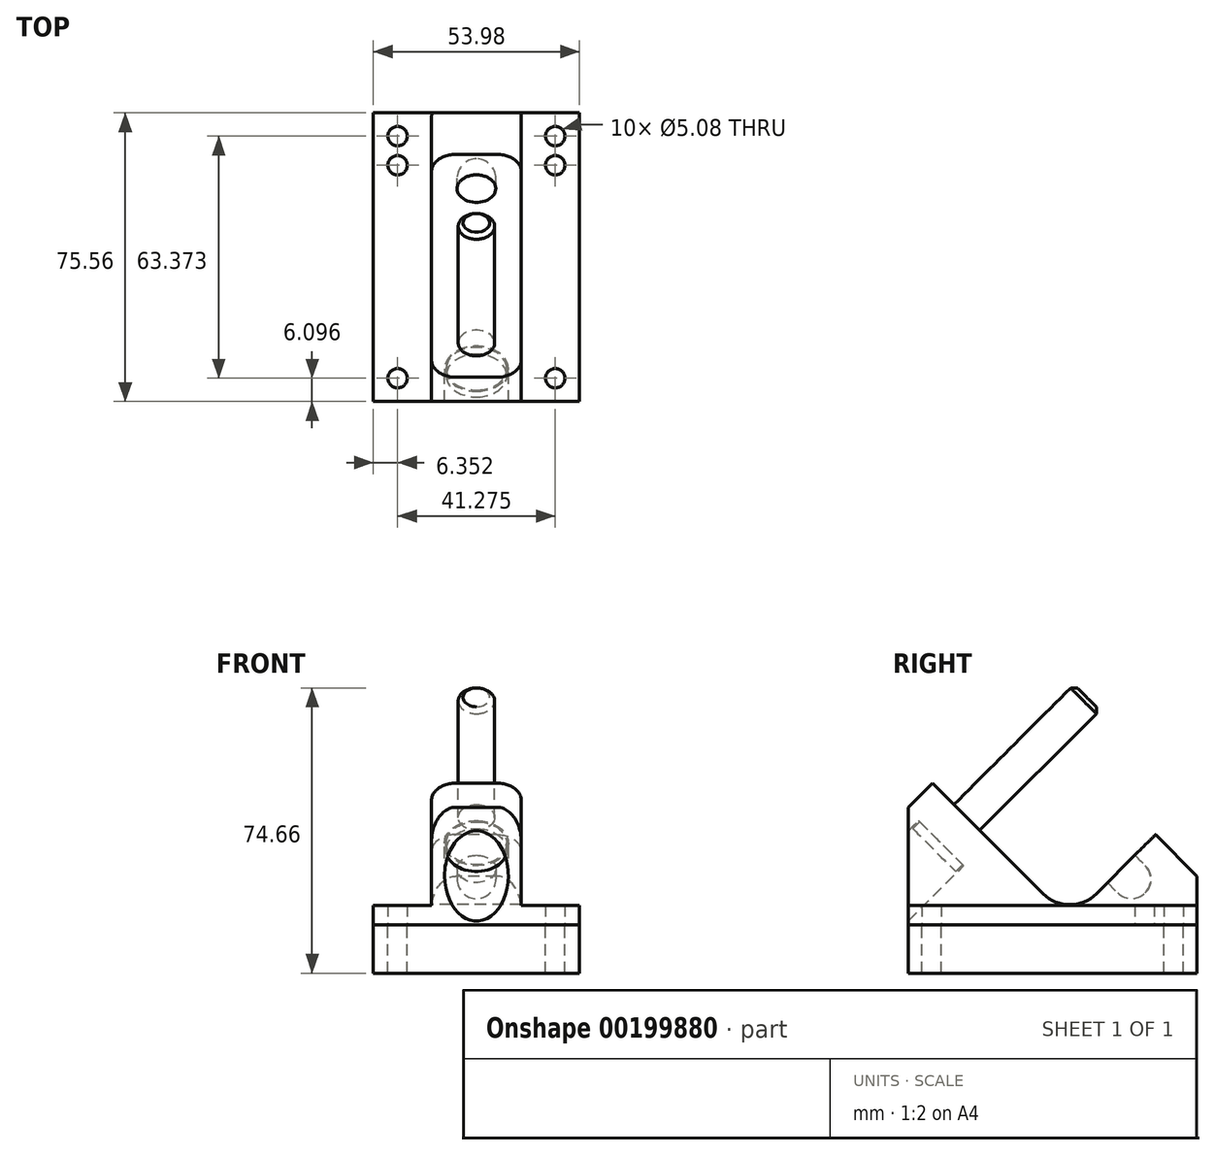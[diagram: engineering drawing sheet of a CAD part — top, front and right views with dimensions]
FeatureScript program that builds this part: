
annotation { "Feature Type Name" : "Feature", "Feature Type Description" : "" }
export const myFeature = defineFeature(function(context is Context, id is Id, definition is map)
    precondition{}
    {
        {
            var Q0;
            Q0=qCreatedBy(makeId("Right.planeOp"),FACE);
            var sketch = newSketch(context, id + "F0", { "sketchPlane" : qUnion([Q0])});
            skLineSegment(sketch, "E0", {"start": v(0, 0) * mm, "end": v(75.57, 0) * mm});
            skLineSegment(sketch, "E1", {"start": v(75.57, 0) * mm, "end": v(75.57, 12.7) * mm});
            skLineSegment(sketch, "E2", {"start": v(75.57, 12.7) * mm, "end": v(64.7, 23.57) * mm});
            skLineSegment(sketch, "E3", {"start": v(64.7, 23.57) * mm, "end": v(42.25, 1.12) * mm});
            skLineSegment(sketch, "E4", {"start": v(0, -14.12) * mm, "end": v(0, 0) * mm, "construction": true});
            skLineSegment(sketch, "E5", {"start": v(0, 0) * mm, "end": v(0, 30.72) * mm});
            skLineSegment(sketch, "E6", {"start": v(0, 30.72) * mm, "end": v(6.32, 37.04) * mm});
            skLineSegment(sketch, "E7", {"start": v(6.32, 37.04) * mm, "end": v(42.25, 1.12) * mm});
            skLineSegment(sketch, "E8", {"start": v(61.1, 19.98) * mm, "end": v(70.08, 11) * mm, "construction": true});
            skLineSegment(sketch, "E9", {"start": v(70.08, 11) * mm, "end": v(59.3, 0.22) * mm, "construction": true});
            skLineSegment(sketch, "E10", {"start": v(59.3, 0.22) * mm, "end": v(50.33, 9.2) * mm, "construction": true});
            skLineSegment(sketch, "E11", {"start": v(64.7, 5.6) * mm, "end": v(15.3, 55) * mm, "construction": true});
            skCircle(sketch, "E12", {"center": v(15.3, 55) * mm, "radius": 4 * mm, "construction": true});
            skLineSegment(sketch, "E13", {"start": v(15.3, 28.06) * mm, "end": v(28.77, 41.53) * mm, "construction": true});
            skCircle(sketch, "E14", {"center": v(58.4, 11.9) * mm, "radius": 5.08 * mm, "construction": true});
            skSolve(sketch);
        }
        {
            var Q0;
            Q0=qSketchRegion(id+"F0",true);
            extrude(context, id + "F1", {"entities" : qUnion([Q0]), "depth" : 26.99 * mm});
        }
        {
            var Q0;
            Q0=makeQuery(id+"F1.opExtrude","SWEPT_EDGE",EDGE,{"disambiguationData":[OSD([sQuery(id+"F0.wireOp",EDGE,"E3"),sQuery(id+"F0.wireOp",EDGE,"E7")])]});
            fillet(context, id + "F2", {"entities" : qUnion([Q0]), "radius" : 9.9 * mm, "tangentPropagation" : true, "allowEdgeOverflow" : false});
        }
        {
            var Q0;
            Q0=makeQuery(id+"F1.opExtrude","CAP_FACE",FACE,{"disambiguationData":[OSD([sQuery(id+"F0.wireOp",EDGE,"E0"),sQuery(id+"F0.wireOp",EDGE,"E1"),sQuery(id+"F0.wireOp",EDGE,"E2"),sQuery(id+"F0.wireOp",EDGE,"E3"),sQuery(id+"F0.wireOp",EDGE,"O8t1L6aE-7V4B-qQYz-aJHa-yxt4Uf4GNHZm"),sQuery(id+"F0.wireOp",EDGE,"dINw5n4X-CGaa-rPGi-QK1T-MrZfrRMsY7ox"),sQuery(id+"F0.wireOp",EDGE,"k2Hi1M4v-dZXO-cidX-ee3S-7WINr6mVTnzP")])],"isStart":false});
            var sketch = newSketch(context, id + "F3", { "sketchPlane" : qUnion([Q0])});
            skLineSegment(sketch, "E15.bottom", {"start": v(75.57, 5.08) * mm, "end": v(0, 5.08) * mm});
            skLineSegment(sketch, "E15.top", {"start": v(75.57, 37.04) * mm, "end": v(0, 37.04) * mm});
            skLineSegment(sketch, "E15.left", {"start": v(75.57, 5.08) * mm, "end": v(75.57, 37.04) * mm});
            skLineSegment(sketch, "E15.right", {"start": v(0, 5.08) * mm, "end": v(0, 37.04) * mm});
            skSolve(sketch);
        }
        {
            var Q0;
            Q0=qSketchRegion(id+"F3",true);
            extrude(context, id + "F4", {"entities" : qUnion([Q0]), "operationType" : NewBodyOperationType.REMOVE, "oppositeDirection" : true, "depth" : 15.24 * mm});
        }
        {
            var Q0;
            Q0=makeQuery(id+"F1.opExtrude","SWEPT_FACE",FACE,{"disambiguationData":[OSD([sQuery(id+"F0.wireOp",EDGE,"E0")])]});
            var sketch = newSketch(context, id + "F5", { "sketchPlane" : qUnion([Q0])});
            skLineSegment(sketch, "E16", {"start": v(20.64, -6.1) * mm, "end": v(20.64, -61.85) * mm, "construction": true});
            skLineSegment(sketch, "E17", {"start": v(20.64, -61.85) * mm, "end": v(20.64, -69.47) * mm, "construction": true});
            skCircle(sketch, "E18", {"center": v(20.64, -6.1) * mm, "radius": 2.54 * mm});
            skCircle(sketch, "E19", {"center": v(20.64, -61.85) * mm, "radius": 2.54 * mm});
            skCircle(sketch, "E20", {"center": v(20.64, -69.47) * mm, "radius": 2.54 * mm});
            skSolve(sketch);
        }
        {
            var Q0;
            Q0=qSketchRegion(id+"F5",true);
            extrude(context, id + "F6", {"entities" : qUnion([Q0]), "operationType" : NewBodyOperationType.REMOVE, "endBound" : BoundingType.UP_TO_NEXT, "oppositeDirection" : true, "depth" : 25.4 * mm});
        }
        {
            var Q0;
            Q0=makeQuery(id+"F1.opExtrude","CAP_FACE",FACE,{"disambiguationData":[OSD([sQuery(id+"F0.wireOp",EDGE,"E0"),sQuery(id+"F0.wireOp",EDGE,"E1"),sQuery(id+"F0.wireOp",EDGE,"E2"),sQuery(id+"F0.wireOp",EDGE,"E3"),sQuery(id+"F0.wireOp",EDGE,"O8t1L6aE-7V4B-qQYz-aJHa-yxt4Uf4GNHZm"),sQuery(id+"F0.wireOp",EDGE,"dINw5n4X-CGaa-rPGi-QK1T-MrZfrRMsY7ox"),sQuery(id+"F0.wireOp",EDGE,"k2Hi1M4v-dZXO-cidX-ee3S-7WINr6mVTnzP")])],"isStart":true});
            var sketch = newSketch(context, id + "F7", { "sketchPlane" : qUnion([Q0])});
            skLineSegment(sketch, "E21", {"start": v(-11.94, 31.43) * mm, "end": v(-5.2, 24.7) * mm});
            skLineSegment(sketch, "E22", {"start": v(-5.2, 24.7) * mm, "end": v(-2.67, 27.22) * mm});
            skLineSegment(sketch, "E23", {"start": v(-2.67, 27.22) * mm, "end": v(12.28, 12.28) * mm});
            skLineSegment(sketch, "E24", {"start": v(12.28, 12.28) * mm, "end": v(6.38, 6.38) * mm});
            skLineSegment(sketch, "E25", {"start": v(6.38, 6.38) * mm, "end": v(-15.3, 28.06) * mm});
            skLineSegment(sketch, "E26", {"start": v(-15.3, 28.06) * mm, "end": v(-16.61, 29.37) * mm, "construction": true});
            skLineSegment(sketch, "E27", {"start": v(-15.3, 28.06) * mm, "end": v(-11.94, 31.43) * mm});
            skLineSegment(sketch, "E28", {"start": v(0, 0) * mm, "end": v(6.38, 6.38) * mm});
            skSolve(sketch);
        }
        {
            var Q0;
            Q0=qSketchRegion(id+"F7",true);
            var Q1;
            Q1=sQuery(id+"F7.wireOp",EDGE,"E25");
            revolve(context, id + "F8", {"operationType" : NewBodyOperationType.REMOVE, "entities" : qUnion([Q0]), "axis" : qUnion([Q1]), "revolveType" : RevolveType.FULL, "oppositeDirection" : true});
        }
        {
            var Q0;
            Q0=qCreatedBy(makeId("Right.planeOp"),FACE);
            var sketch = newSketch(context, id + "F9", { "sketchPlane" : qUnion([Q0])});
            skLineSegment(sketch, "E29", {"start": v(2.96, 26.94) * mm, "end": v(5.2, 24.7) * mm});
            skLineSegment(sketch, "E30", {"start": v(5.2, 24.7) * mm, "end": v(43.37, 62.86) * mm});
            skLineSegment(sketch, "E31", {"start": v(43.37, 62.86) * mm, "end": v(46.74, 59.5) * mm});
            skLineSegment(sketch, "E32", {"start": v(46.74, 59.5) * mm, "end": v(6.77, 19.53) * mm});
            skLineSegment(sketch, "E33", {"start": v(6.77, 19.53) * mm, "end": v(1.16, 25.14) * mm});
            skLineSegment(sketch, "E34", {"start": v(1.16, 25.14) * mm, "end": v(2.96, 26.94) * mm});
            skLineSegment(sketch, "E35", {"start": v(6.77, 19.53) * mm, "end": v(2.3, 15.06) * mm, "construction": true});
            skPoint(sketch, "E36", {"position": v(8.78, 21.53) * mm});
            skSolve(sketch);
        }
        {
            var Q0;
            Q0=qSketchRegion(id+"F9",true);
            var Q1;
            Q1=sQuery(id+"F9.wireOp",EDGE,"E32");
            revolve(context, id + "F10", {"entities" : qUnion([Q0]), "axis" : qUnion([Q1]), "revolveType" : RevolveType.FULL});
        }
        {
            var Q0;
            Q0=makeQuery(id+"F4.boolean.opBoolean","INTERSECT",EDGE,{"derivedFrom":[makeQuery(id+"F1.opExtrude","SWEPT_FACE",FACE,{"disambiguationData":[OSD([sQuery(id+"F0.wireOp",EDGE,"E2")])]}),makeQuery(id+"F4.opExtrude","CAP_FACE",FACE,{"disambiguationData":[OSD([sQuery(id+"F3.wireOp",EDGE,"E15.bottom"),sQuery(id+"F3.wireOp",EDGE,"E15.top"),sQuery(id+"F3.wireOp",EDGE,"E15.left"),sQuery(id+"F3.wireOp",EDGE,"E15.right")])],"isStart":false})]});
            var Q1;
            Q1=makeQuery(id+"FPWNDdPn0RB2iZ7_1.opPattern","COPY",EDGE,{"derivedFrom":makeQuery(id+"F4.boolean.opBoolean","INTERSECT",EDGE,{"derivedFrom":[makeQuery(id+"F1.opExtrude","SWEPT_FACE",FACE,{"disambiguationData":[OSD([sQuery(id+"F0.wireOp",EDGE,"E2")])]}),makeQuery(id+"F4.opExtrude","CAP_FACE",FACE,{"disambiguationData":[OSD([sQuery(id+"F3.wireOp",EDGE,"E15.bottom"),sQuery(id+"F3.wireOp",EDGE,"E15.top"),sQuery(id+"F3.wireOp",EDGE,"E15.left"),sQuery(id+"F3.wireOp",EDGE,"E15.right")])],"isStart":false})]}),"instanceName":"1"});
            var Q2;
            Q2=makeQuery(id+"F4.boolean.opBoolean","INTERSECT",EDGE,{"derivedFrom":[makeQuery(id+"F1.opExtrude","SWEPT_FACE",FACE,{"disambiguationData":[OSD([sQuery(id+"F0.wireOp",EDGE,"E6")])]}),makeQuery(id+"F4.opExtrude","CAP_FACE",FACE,{"disambiguationData":[OSD([sQuery(id+"F3.wireOp",EDGE,"E15.bottom"),sQuery(id+"F3.wireOp",EDGE,"E15.top"),sQuery(id+"F3.wireOp",EDGE,"E15.left"),sQuery(id+"F3.wireOp",EDGE,"E15.right")])],"isStart":false})]});
            var Q3;
            Q3=makeQuery(id+"FPWNDdPn0RB2iZ7_1.opPattern","COPY",EDGE,{"derivedFrom":makeQuery(id+"F4.boolean.opBoolean","INTERSECT",EDGE,{"derivedFrom":[makeQuery(id+"F1.opExtrude","SWEPT_FACE",FACE,{"disambiguationData":[OSD([sQuery(id+"F0.wireOp",EDGE,"E6")])]}),makeQuery(id+"F4.opExtrude","CAP_FACE",FACE,{"disambiguationData":[OSD([sQuery(id+"F3.wireOp",EDGE,"E15.bottom"),sQuery(id+"F3.wireOp",EDGE,"E15.top"),sQuery(id+"F3.wireOp",EDGE,"E15.left"),sQuery(id+"F3.wireOp",EDGE,"E15.right")])],"isStart":false})]}),"instanceName":"1"});
            fillet(context, id + "F11", {"entities" : qUnion([Q0, Q1, Q2, Q3]), "radius" : 6.35 * mm, "tangentPropagation" : true, "allowEdgeOverflow" : false});
        }
        {
            var Q0;
            Q0=qCreatedBy(makeId("Right.planeOp"),FACE);
            var sketch = newSketch(context, id + "F12", { "sketchPlane" : qUnion([Q0])});
            skLineSegment(sketch, "E37.0", {"start": v(61.1, 19.98) * mm, "end": v(70.08, 11) * mm});
            skLineSegment(sketch, "E37.1", {"start": v(70.08, 11) * mm, "end": v(64.7, 5.6) * mm});
            skLineSegment(sketch, "E37.2", {"start": v(64.7, 5.6) * mm, "end": v(55.72, 14.59) * mm});
            skLineSegment(sketch, "E38", {"start": v(61.1, 19.98) * mm, "end": v(55.72, 14.59) * mm});
            skPoint(sketch, "E39.orphan", {"position": v(15.3, 55) * mm});
            skPoint(sketch, "E40.orphan", {"position": v(59.3, 0.22) * mm});
            skSolve(sketch);
        }
        {
            var Q0;
            Q0 = qSketchRegion(id + "F12", true);
            var Q1;
            Q1=sQuery(id+"F12.wireOp",EDGE,"E37.2");
            revolve(context, id + "F13", {"operationType" : NewBodyOperationType.REMOVE, "entities" : qUnion([Q0]), "axis" : qUnion([Q1]), "revolveType" : RevolveType.FULL, "oppositeDirection" : true});
        }
        {
            var Q0;
            Q0=qCreatedBy(makeId("Right.planeOp"),FACE);
            var sketch = newSketch(context, id + "F14", { "sketchPlane" : qUnion([Q0])});
            skLineSegment(sketch, "E41.0", {"start": v(61.1, 19.98) * mm, "end": v(70.08, 11) * mm});
            skLineSegment(sketch, "E41.1", {"start": v(70.08, 11) * mm, "end": v(64.7, 5.6) * mm});
            skLineSegment(sketch, "E41.2", {"start": v(64.7, 5.6) * mm, "end": v(62, 8.3) * mm});
            skArc(sketch, "E41.3", {"start": v(62, 8.3) * mm, "mid": v(63.49, 11.9) * mm, "end": v(62, 15.49) * mm});
            skLineSegment(sketch, "E42", {"start": v(62, 15.49) * mm, "end": v(59.3, 18.18) * mm});
            skLineSegment(sketch, "E43", {"start": v(59.3, 18.18) * mm, "end": v(61.1, 19.98) * mm});
            skPoint(sketch, "E44.orphan", {"position": v(15.3, 55) * mm});
            skPoint(sketch, "E45.orphan", {"position": v(59.3, 0.22) * mm});
            skSolve(sketch);
        }
        {
            var Q0;
            Q0 = qSketchRegion(id + "F14", true);
            var Q1;
            Q1=sQuery(id+"F0.wireOp",EDGE,"E11");
            revolve(context, id + "F15", {"entities" : qUnion([Q0]), "axis" : qUnion([Q1]), "revolveType" : RevolveType.FULL});
        }
        {
            var Q0;
            Q0=makeQuery(id+"F1.opExtrude","SWEPT_BODY",BODY,{"disambiguationData":[OSD([sQuery(id+"F0.wireOp",EDGE,"E0"),sQuery(id+"F0.wireOp",EDGE,"E1"),sQuery(id+"F0.wireOp",EDGE,"E2"),sQuery(id+"F0.wireOp",EDGE,"E3"),sQuery(id+"F0.wireOp",EDGE,"E5"),sQuery(id+"F0.wireOp",EDGE,"E6"),sQuery(id+"F0.wireOp",EDGE,"E7")])]});
            var Q1;
            Q1=qCreatedBy(makeId("Right.planeOp"),FACE);
            mirror(context, id + "F16", {"operationType" : NewBodyOperationType.ADD, "entities" : qUnion([Q0]), "mirrorPlane" : qUnion([Q1])});
        }
        {
            var Q0;
            Q0=makeQuery(id+"F10.opRevolve","SWEPT_EDGE",EDGE,{"disambiguationData":[OSD([sQuery(id+"F9.wireOp",EDGE,"E30"),sQuery(id+"F9.wireOp",EDGE,"E31")])]});
            chamfer(context, id + "F17", {"entities" : qUnion([Q0]), "width" : 1.27 * mm, "tangentPropagation" : true});
        }
        {
            var Q0;
            {var subQ0=makeQuery(id+"F1.opExtrude","SWEPT_FACE",FACE,{"disambiguationData":[OSD([sQuery(id+"F0.wireOp",EDGE,"E0")])]});Q0=makeQuery(id+"F16.boolean.opBoolean","MERGE",FACE,{"derivedFrom":[subQ0,makeQuery(id+"F16.opPattern","COPY",FACE,{"derivedFrom":subQ0,"instanceName":"1"})]});}
            var sketch = newSketch(context, id + "F18", { "sketchPlane" : qUnion([Q0])});
            skLineSegment(sketch, "E46.0", {"start": v(26.99, 0) * mm, "end": v(-26.99, 0) * mm});
            skLineSegment(sketch, "E46.1", {"start": v(26.99, 0) * mm, "end": v(26.99, -75.57) * mm});
            skLineSegment(sketch, "E46.2", {"start": v(26.99, -75.57) * mm, "end": v(-26.99, -75.57) * mm});
            skLineSegment(sketch, "E46.3", {"start": v(-26.99, 0) * mm, "end": v(-26.99, -75.57) * mm});
            skCircle(sketch, "E46.4", {"center": v(-20.64, -69.47) * mm, "radius": 2.54 * mm});
            skCircle(sketch, "E46.5", {"center": v(20.64, -69.47) * mm, "radius": 2.54 * mm});
            skCircle(sketch, "E46.6", {"center": v(20.64, -6.1) * mm, "radius": 2.54 * mm});
            skCircle(sketch, "E46.7", {"center": v(-20.64, -6.1) * mm, "radius": 2.54 * mm});
            skSolve(sketch);
        }
        {
            var Q0;
            Q0 = qSketchRegion(id + "F18", true);
            extrude(context, id + "F19", {"entities" : qUnion([Q0]), "depth" : 12.7 * mm});
        }
    });
